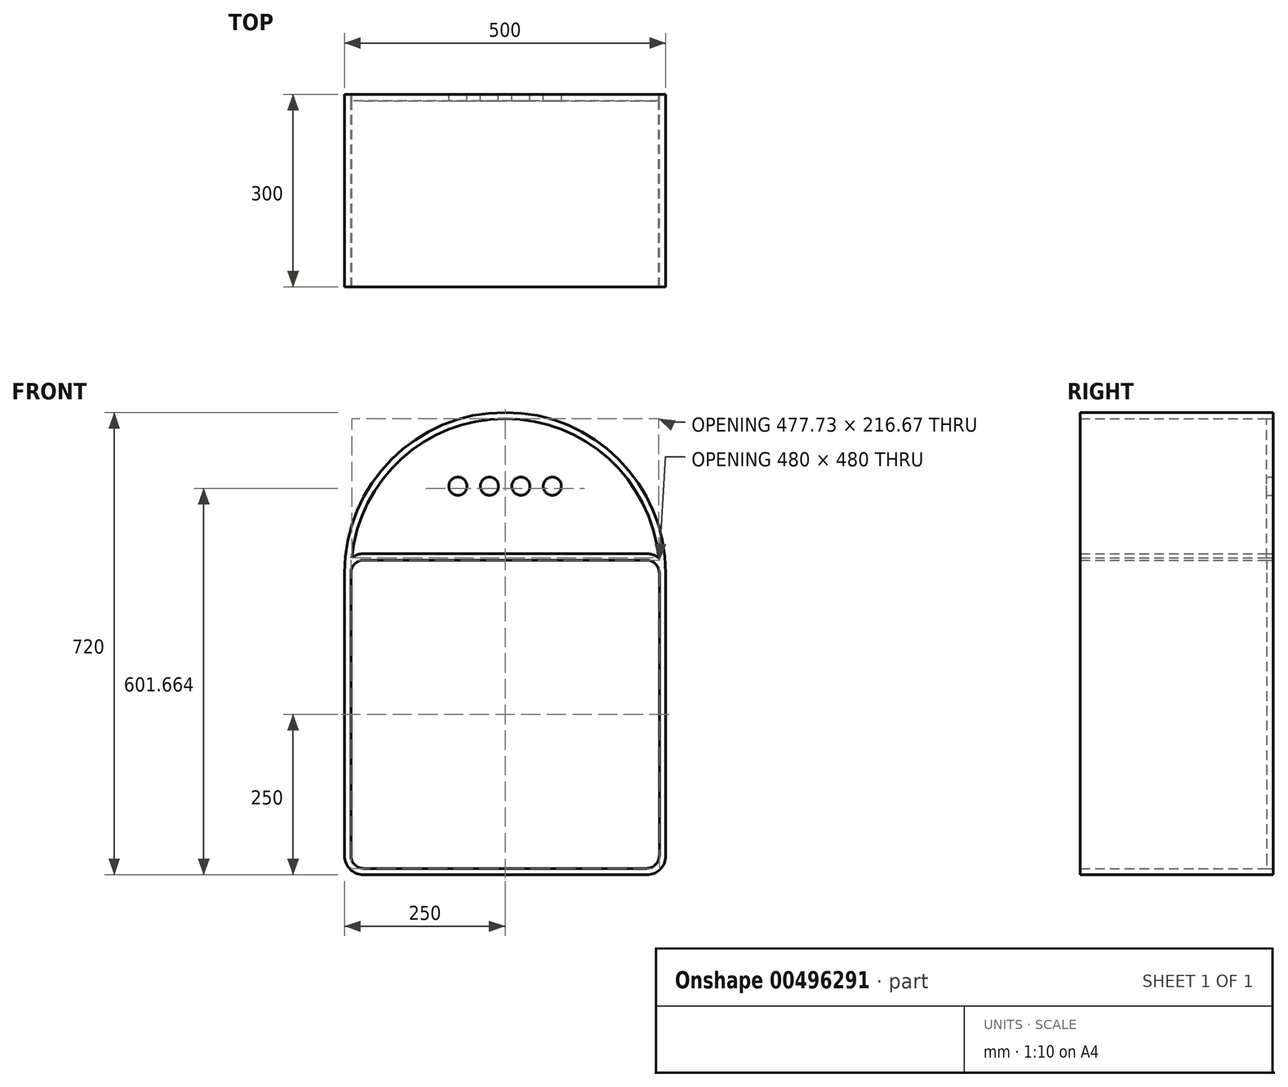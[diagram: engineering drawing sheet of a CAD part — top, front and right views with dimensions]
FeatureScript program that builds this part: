
annotation { "Feature Type Name" : "Feature", "Feature Type Description" : "" }
export const myFeature = defineFeature(function(context is Context, id is Id, definition is map)
    precondition{}
    {
        {
            var Q0;
            Q0=qCreatedBy(makeId("Front.planeOp"),FACE);
            var sketch = newSketch(context, id + "F0", { "sketchPlane" : qUnion([Q0])});
            skLineSegment(sketch, "E0.bottom", {"start": v(-220, 250) * mm, "end": v(220, 250) * mm});
            skLineSegment(sketch, "E0.top", {"start": v(-220, -250) * mm, "end": v(220, -250) * mm});
            skLineSegment(sketch, "E0.left", {"start": v(-250, 220) * mm, "end": v(-250, -220) * mm});
            skLineSegment(sketch, "E0.right", {"start": v(250, 220) * mm, "end": v(250, -220) * mm});
            skPoint(sketch, "E0.middle", {"position": v(0, 0) * mm});
            skPoint(sketch, "E1.visualSharp", {"position": v(-250, 250) * mm});
            skArc(sketch, "E1.filletArc", {"start": v(-220, 250) * mm, "mid": v(-241.21, 241.21) * mm, "end": v(-250, 220) * mm});
            skPoint(sketch, "E2.visualSharp", {"position": v(250, 250) * mm});
            skArc(sketch, "E2.filletArc", {"start": v(250, 220) * mm, "mid": v(241.21, 241.21) * mm, "end": v(220, 250) * mm});
            skPoint(sketch, "E3.visualSharp", {"position": v(250, -250) * mm});
            skArc(sketch, "E3.filletArc", {"start": v(220, -250) * mm, "mid": v(241.21, -241.21) * mm, "end": v(250, -220) * mm});
            skPoint(sketch, "E4.visualSharp", {"position": v(-250, -250) * mm});
            skArc(sketch, "E4.filletArc", {"start": v(-250, -220) * mm, "mid": v(-241.21, -241.21) * mm, "end": v(-220, -250) * mm});
            skArc(sketch, "E5", {"start": v(250, 220) * mm, "mid": v(0, 470) * mm, "end": v(-250, 220) * mm});
            skArc(sketch, "E6.0", {"start": v(-220, 240) * mm, "mid": v(-234.14, 234.14) * mm, "end": v(-240, 220) * mm});
            skLineSegment(sketch, "E6.1", {"start": v(-220, 240) * mm, "end": v(220, 240) * mm});
            skLineSegment(sketch, "E6.2", {"start": v(-240, 220) * mm, "end": v(-240, -220) * mm});
            skArc(sketch, "E6.3", {"start": v(240, 220) * mm, "mid": v(234.14, 234.14) * mm, "end": v(220, 240) * mm});
            skArc(sketch, "E6.4", {"start": v(-240, -220) * mm, "mid": v(-234.14, -234.14) * mm, "end": v(-220, -240) * mm});
            skLineSegment(sketch, "E6.5", {"start": v(-220, -240) * mm, "end": v(220, -240) * mm});
            skArc(sketch, "E6.6", {"start": v(220, -240) * mm, "mid": v(234.14, -234.14) * mm, "end": v(240, -220) * mm});
            skLineSegment(sketch, "E6.7", {"start": v(240, 220) * mm, "end": v(240, -220) * mm});
            skArc(sketch, "E7.0", {"start": v(238.86, 243.33) * mm, "mid": v(0, 460) * mm, "end": v(-238.86, 243.33) * mm});
            skPoint(sketch, "E8.endSnap0", {"position": v(0, 460) * mm});
            skCircle(sketch, "E9", {"center": v(-24.49, 355) * mm, "radius": 14.15 * mm});
            skCircle(sketch, "E10", {"center": v(24.48, 355) * mm, "radius": 14.15 * mm});
            skCircle(sketch, "E11", {"center": v(-73.46, 355) * mm, "radius": 14.15 * mm});
            skCircle(sketch, "E12", {"center": v(73.45, 355) * mm, "radius": 14.15 * mm});
            skPoint(sketch, "E8.end.orphan", {"position": v(0, 355) * mm});
            skPoint(sketch, "E8.start.orphan", {"position": v(0, 460) * mm});
            skSolve(sketch);
        }
        {
            var Q0;
            Q0=makeQuery(id+"F0.imprint","IMPRINT",FACE,{"disambiguationData":[TD([[makeQuery(id+"F0.imprint","IMPRINT",EDGE,{"derivedFrom":sQuery(id+"F0.wireOp",EDGE,"E6.0")}),1.0]])]});
            var Q1;
            {var subQ1=sQuery(id+"F0.wireOp",EDGE,"E0.bottom");Q1=makeQuery(id+"F0.imprint","IMPRINT",FACE,{"disambiguationData":[TD([[makeQuery(id+"F0.imprint","IMPRINT",EDGE,{"derivedFrom":subQ1}),1.0]])]});}
            extrude(context, id + "F1", {"entities" : qUnion([Q0, Q1]), "depth" : 10 * mm, "offsetDistance" : 25 * mm});
        }
        {
            var Q0;
            Q0 = qSketchRegion(id + "F0", true);
            extrude(context, id + "F2", {"entities" : qUnion([Q0]), "depth" : 300 * mm, "offsetDistance" : 25 * mm});
        }
    });
